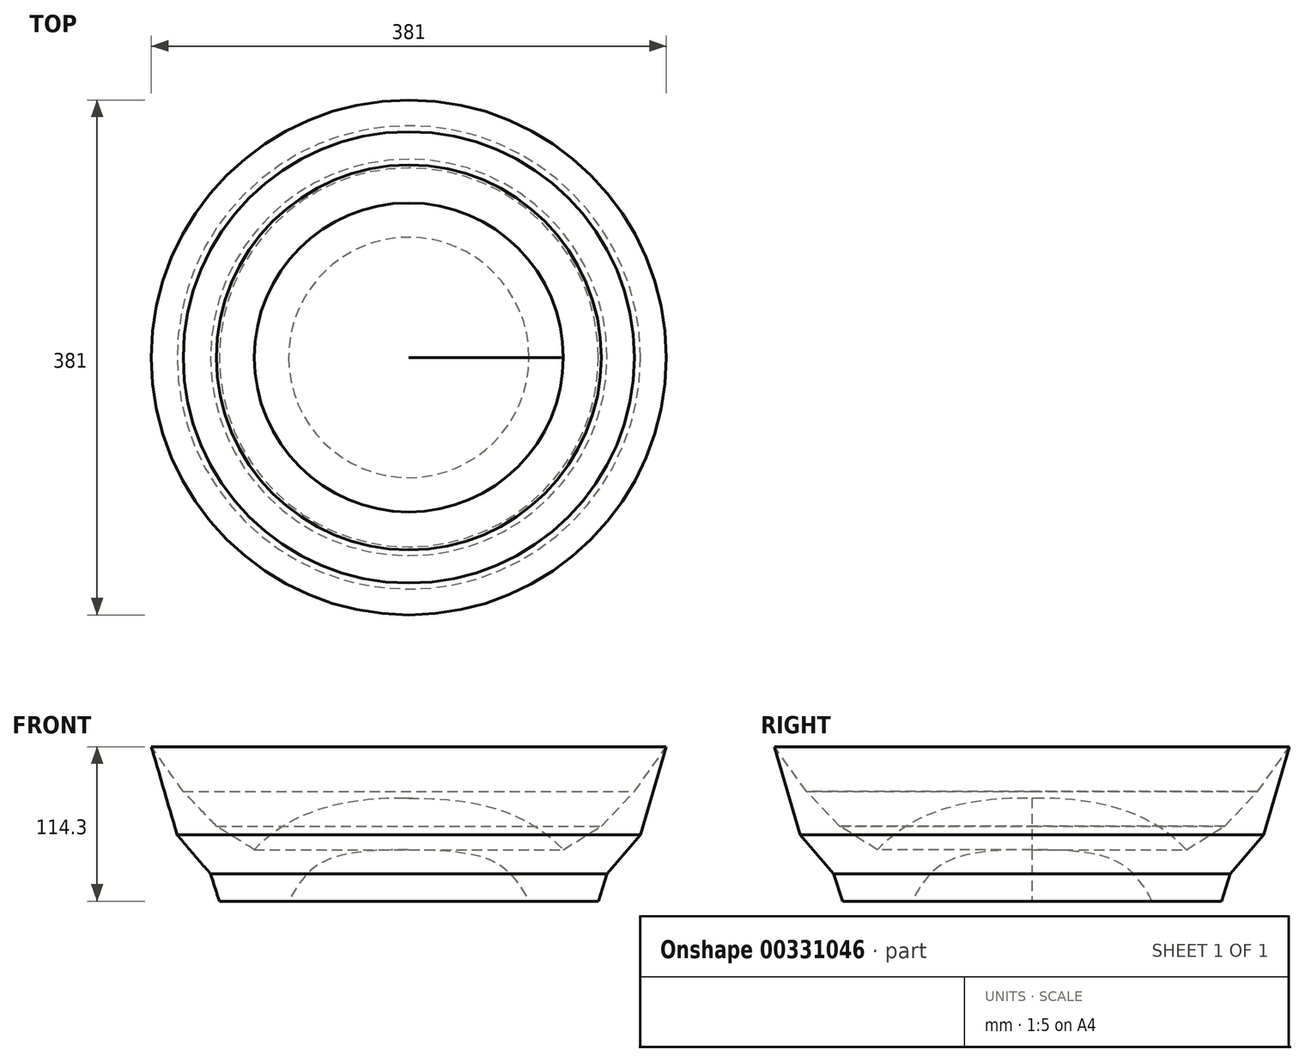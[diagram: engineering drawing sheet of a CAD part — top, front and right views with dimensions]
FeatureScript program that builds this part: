
annotation { "Feature Type Name" : "Feature", "Feature Type Description" : "" }
export const myFeature = defineFeature(function(context is Context, id is Id, definition is map)
    precondition{}
    {
        {
            var Q0;
            Q0=qCreatedBy(makeId("Front.planeOp"),FACE);
            var sketch = newSketch(context, id + "F0", { "sketchPlane" : qUnion([Q0])});
            skLineSegment(sketch, "E0.bottom", {"start": v(-60.26, 114.3) * mm, "end": v(130.24, 114.3) * mm, "construction": true});
            skLineSegment(sketch, "E0.top", {"start": v(-60.26, 0) * mm, "end": v(130.24, 0) * mm, "construction": true});
            skLineSegment(sketch, "E0.left", {"start": v(-60.26, 114.3) * mm, "end": v(-60.26, 0) * mm, "construction": true});
            skLineSegment(sketch, "E0.right", {"start": v(130.24, 114.3) * mm, "end": v(130.24, 0) * mm, "construction": true});
            skLineSegment(sketch, "E1", {"start": v(-60.26, 0) * mm, "end": v(28.64, 0) * mm});
            skLineSegment(sketch, "E2", {"start": v(-60.26, 0) * mm, "end": v(-60.26, 38.1) * mm, "construction": true});
            skLineSegment(sketch, "E3", {"start": v(-60.26, 38.1) * mm, "end": v(-60.26, 76.2) * mm});
            skFitSpline(sketch, "E4", {"points": [v(-60.26, 38.1) * mm, v(28.64, 0) * mm], "startDerivative": vector(180.79, 0) * mm, "endDerivative": vector(47.64, -88.44) * mm});
            skLineSegment(sketch, "E5", {"start": v(28.64, 0) * mm, "end": v(54.04, 0) * mm});
            skLineSegment(sketch, "E6", {"start": v(-60.26, 38.1) * mm, "end": v(54.04, 38.1) * mm, "construction": true});
            skFitSpline(sketch, "E7", {"points": [v(-60.26, 76.2) * mm, v(54.04, 38.1) * mm], "startDerivative": vector(136.12, 1.28) * mm, "endDerivative": vector(85.33, -90.57) * mm});
            skLineSegment(sketch, "E8", {"start": v(54.04, 0) * mm, "end": v(86.41, 20.09) * mm, "construction": true});
            skLineSegment(sketch, "E9", {"start": v(86.41, 20.09) * mm, "end": v(111.16, 49.06) * mm});
            skLineSegment(sketch, "E10", {"start": v(54.04, 0) * mm, "end": v(54.04, 38.1) * mm, "construction": true});
            skLineSegment(sketch, "E11", {"start": v(54.04, 38.1) * mm, "end": v(82.1, 55.5) * mm});
            skLineSegment(sketch, "E12", {"start": v(82.1, 55.5) * mm, "end": v(106.65, 81.23) * mm});
            skLineSegment(sketch, "E13", {"start": v(111.16, 49.06) * mm, "end": v(130.24, 114.3) * mm});
            skLineSegment(sketch, "E14", {"start": v(106.65, 81.23) * mm, "end": v(130.24, 114.3) * mm});
            skLineSegment(sketch, "E15", {"start": v(28.64, 0) * mm, "end": v(79.92, 0) * mm});
            skLineSegment(sketch, "E16", {"start": v(79.92, 0) * mm, "end": v(86.41, 20.09) * mm});
            skSolve(sketch);
        }
        {
            var Q0;
            Q0=makeQuery(id+"F0.imprint","IMPRINT",FACE,{"disambiguationData":[TD([[makeQuery(id+"F0.imprint","IMPRINT",EDGE,{"derivedFrom":sQuery(id+"F0.wireOp",EDGE,"E3")}),-1.0]])]});
            var Q1;
            Q1=sQuery(id+"F0.wireOp",EDGE,"E3");
            revolve(context, id + "F1", {"entities" : qUnion([Q0]), "axis" : qUnion([Q1]), "revolveType" : RevolveType.FULL});
        }
    });
